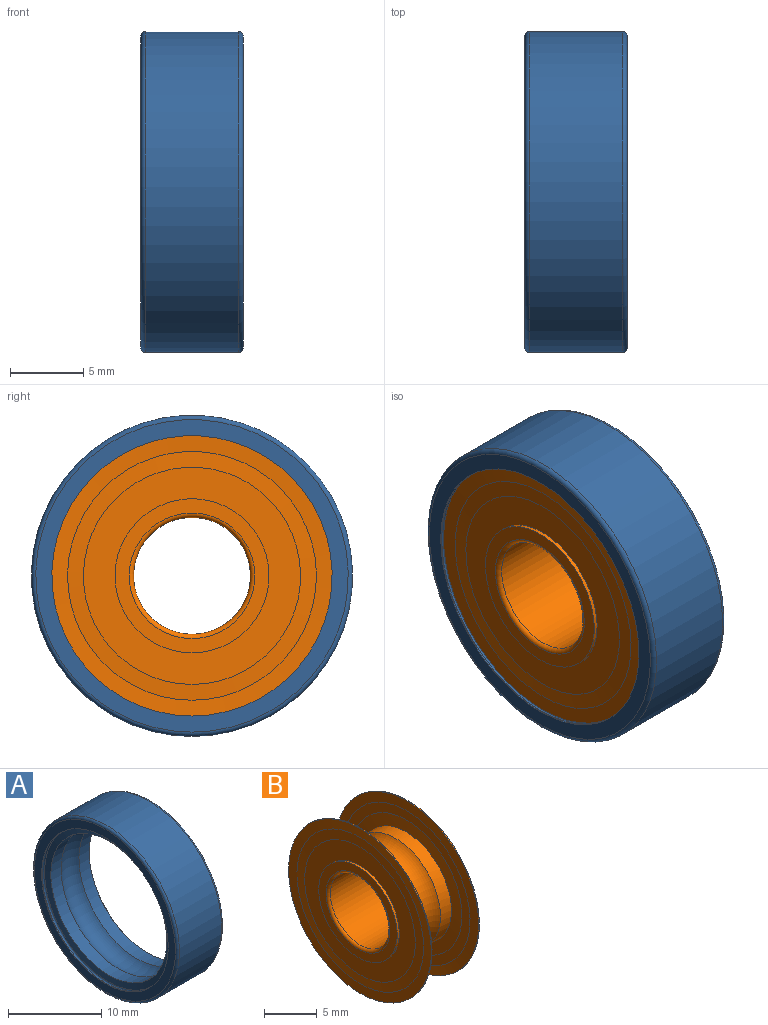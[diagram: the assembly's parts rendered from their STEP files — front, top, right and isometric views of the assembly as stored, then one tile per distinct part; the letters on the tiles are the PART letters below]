
ASSEMBLY  parts=2 mates=1
PART A: 14 faces, bbox 7x23.8x23.8 mm
  f0: plane 21.4x21.4mm, normal (-1,0,0), area 70.2mm2, adj f1,f13
  f1: cylinder r=9.6mm len=19.2mm, axis (-1,0,0), area 5.4mm2, adj f0,f2
  f2: torus R=9.6mm, axis (1,0,0), area 34.5mm2, adj f1,f3
  f3: cone r=9.6mm half-angle=80deg, axis (-1,0,0), area 47mm2, adj f2,f4
  f4: cylinder r=8.8mm len=17.6mm, axis (-1,0,0), area 85.9mm2, adj f3,f5
  f5: torus R=7.35mm, axis (1,0,0), area 171.5mm2, adj f4,f6
  f6: cylinder r=8.8mm len=17.6mm, axis (-1,0,0), area 85.9mm2, adj f5,f7
  f7: cone r=8.8mm half-angle=80deg, axis (1,0,0), area 47mm2, adj f6,f8
  f8: torus R=9.6mm, axis (1,0,0), area 34.5mm2, adj f7,f9
  f9: cylinder r=9.6mm len=19.2mm, axis (-1,0,0), area 5.4mm2, adj f8,f10
  f10: plane 21.4x21.4mm, normal (1,0,0), area 70.2mm2, adj f9,f11
  f11: torus R=10.7mm, axis (1,0,0), area 32.2mm2, adj f10,f12
  f12: cylinder r=11mm len=22mm, axis (-1,0,0), area 442.3mm2, adj f11,f13
  f13: torus R=10.7mm, axis (1,0,0), area 32.2mm2, adj f0,f12
PART B: 28 faces, bbox 7x19.2x19.2 mm
  f0: cone r=9.6mm half-angle=85.2deg, axis (1,0,0), area 61.8mm2, adj f1,f27
  f1: plane 17.04x17.04mm, normal (-1,0,0), area 54.2mm2, adj f0,f2
  f2: cone r=7.44mm half-angle=87.6deg, axis (-1,0,0), area 86mm2, adj f1,f15
  f3: plane 10.55x10.55mm, normal (-1,0,0), area 29.3mm2, adj f5,f12
  f4: plane 10.55x10.55mm, normal (1,0,0), area 29.3mm2, adj f7,f13
  f5: cylinder r=5.28mm len=10.55mm, axis (-1,0,0), area 8.9mm2, adj f3,f20
  f6: torus R=5.5mm, axis (1,0,0), area 9.3mm2, adj f16,f21
  f7: torus R=4.3mm, axis (1,0,0), area 12.2mm2, adj f4,f11
  f8: cylinder r=6.07mm len=12.15mm, axis (-1,0,0), area 56.1mm2, adj f9,f16
  f9: torus R=7.35mm, axis (1,0,0), area 122.1mm2, adj f8,f10
  f10: cylinder r=6.07mm len=12.15mm, axis (-1,0,0), area 56.1mm2, adj f9,f14
  f11: cylinder r=4mm len=8mm, axis (-1,0,0), area 160.8mm2, adj f7,f12
  f12: torus R=4.3mm, axis (1,0,0), area 12.2mm2, adj f3,f11
  f13: cylinder r=5.28mm len=10.55mm, axis (-1,0,0), area 8.9mm2, adj f4,f24
  f14: plane 12.15x12.15mm, normal (1,0,0), area 20.9mm2, adj f10,f15
  f15: torus R=5.5mm, axis (1,0,0), area 9.3mm2, adj f2,f14
  f16: plane 12.15x12.15mm, normal (-1,0,0), area 20.9mm2, adj f6,f8
  f17: cylinder r=9.6mm len=19.2mm, axis (-1,0,0), area 5.4mm2, adj f18,f23
  f18: cone r=9.6mm half-angle=87.6deg, axis (-1,0,0), area 61.6mm2, adj f17,f19
  f19: cone r=8.52mm half-angle=87.6deg, axis (1,0,0), area 54.2mm2, adj f18,f20
  f20: plane 14.88x14.88mm, normal (-1,0,0), area 86.4mm2, adj f5,f19
  f21: cone r=5.28mm half-angle=87.6deg, axis (1,0,0), area 86mm2, adj f6,f22
  f22: plane 17.04x17.04mm, normal (1,0,0), area 54.2mm2, adj f21,f23
  f23: cone r=8.52mm half-angle=85.2deg, axis (-1,0,0), area 61.8mm2, adj f17,f22
  f24: plane 14.88x14.88mm, normal (1,0,0), area 86.4mm2, adj f13,f25
  f25: cone r=7.44mm half-angle=87.6deg, axis (-1,0,0), area 54.2mm2, adj f24,f26
  f26: cone r=8.52mm half-angle=87.6deg, axis (1,0,0), area 61.6mm2, adj f25,f27
  f27: cylinder r=9.6mm len=19.2mm, axis (-1,0,0), area 5.4mm2, adj f0,f26
PLACE A t=(1.53,0.84,3.6)mm
PLACE B t=(1.53,0.84,3.6)mm
MATE fastened B.f0 <-> A.f1  axis (-1,0,0) through (5.03,0.84,3.6)mm
